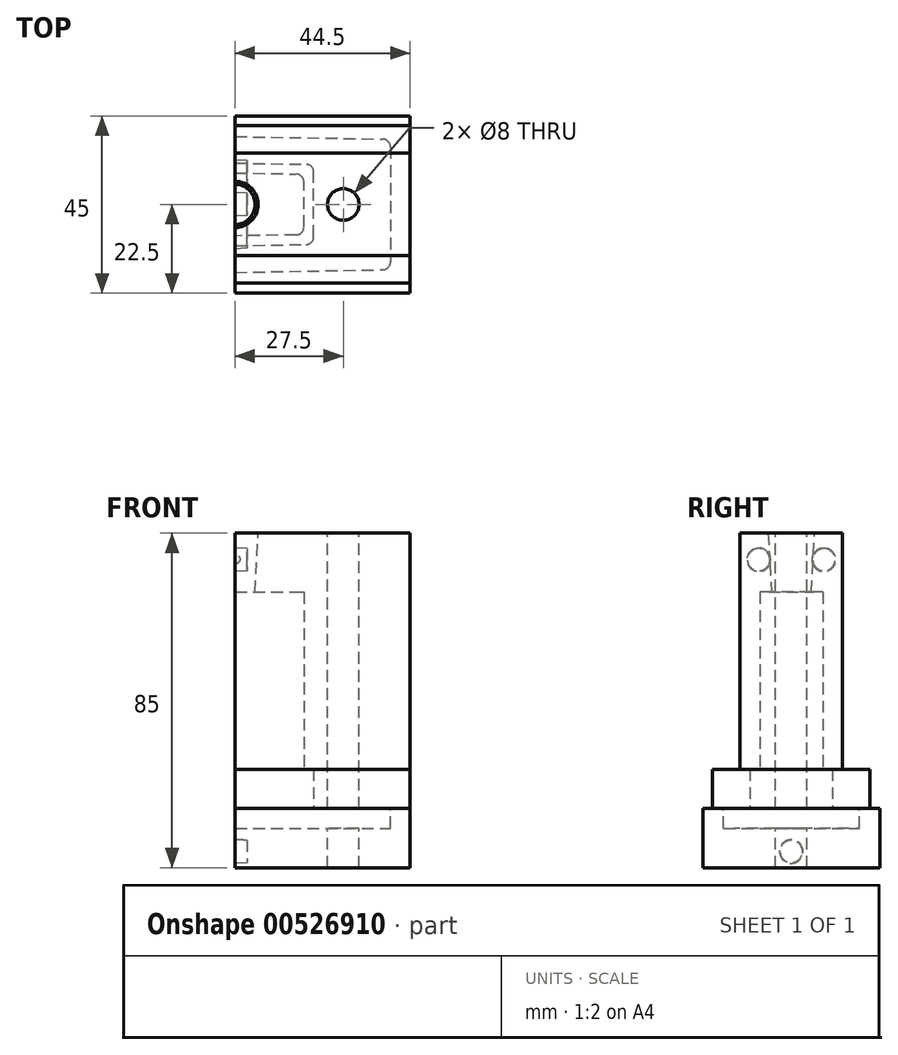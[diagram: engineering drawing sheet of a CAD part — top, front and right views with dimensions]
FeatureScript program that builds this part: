
annotation { "Feature Type Name" : "Feature", "Feature Type Description" : "" }
export const myFeature = defineFeature(function(context is Context, id is Id, definition is map)
    precondition{}
    {
        {
            var Q0;
            Q0=qCreatedBy(makeId("Top.planeOp"),FACE);
            var sketch = newSketch(context, id + "F0", { "sketchPlane" : qUnion([Q0])});
            skLineSegment(sketch, "E0.bottom", {"start": v(44.4, -13) * mm, "end": v(-44.4, -13) * mm});
            skLineSegment(sketch, "E0.top", {"start": v(44.4, 13) * mm, "end": v(-44.4, 13) * mm});
            skLineSegment(sketch, "E0.left", {"start": v(44.4, -13) * mm, "end": v(44.4, 13) * mm});
            skLineSegment(sketch, "E0.right", {"start": v(-44.4, -13) * mm, "end": v(-44.4, 13) * mm});
            skPoint(sketch, "E0.middle", {"position": v(0, 0) * mm});
            skSolve(sketch);
        }
        {
            var Q0;
            Q0=qSketchRegion(id+"F0",true);
            extrude(context, id + "F1", {"entities" : qUnion([Q0]), "depth" : 60 * mm, "offsetDistance" : 25 * mm});
        }
        {
            var Q0;
            Q0=makeQuery(id+"F1.opExtrude","CAP_FACE",FACE,{"disambiguationData":[OSD([sQuery(id+"F0.wireOp",EDGE,"E0.bottom"),sQuery(id+"F0.wireOp",EDGE,"E0.top"),sQuery(id+"F0.wireOp",EDGE,"E0.left"),sQuery(id+"F0.wireOp",EDGE,"E0.right")])],"isStart":true});
            var sketch = newSketch(context, id + "F2", { "sketchPlane" : qUnion([Q0])});
            skPoint(sketch, "E1.middle", {"position": v(0, 0) * mm});
            skLineSegment(sketch, "E2", {"start": v(0, -8) * mm, "end": v(-17.5, -7.7) * mm});
            skLineSegment(sketch, "E3", {"start": v(0, -8) * mm, "end": v(17.5, -7.7) * mm});
            skLineSegment(sketch, "E4", {"start": v(0, 8) * mm, "end": v(-17.5, 7.7) * mm});
            skLineSegment(sketch, "E5", {"start": v(17.5, 7.7) * mm, "end": v(0, 8) * mm});
            skLineSegment(sketch, "E6", {"start": v(-17.5, 7.7) * mm, "end": v(-17.5, -7.7) * mm});
            skLineSegment(sketch, "E7", {"start": v(17.5, 7.7) * mm, "end": v(17.5, -7.7) * mm});
            skSolve(sketch);
        }
        {
            var Q0;
            Q0=qSketchRegion(id+"F2",true);
            extrude(context, id + "F3", {"entities" : qUnion([Q0]), "operationType" : NewBodyOperationType.REMOVE, "oppositeDirection" : true, "depth" : 45 * mm, "offsetDistance" : 25 * mm});
        }
        {
            var Q0;
            Q0=makeQuery(id+"F3.boolean.opBoolean","COPY",EDGE,{"derivedFrom":makeQuery(id+"F3.opExtrude","SWEPT_EDGE",EDGE,{"disambiguationData":[OSD([sQuery(id+"F2.wireOp",EDGE,"E2"),sQuery(id+"F2.wireOp",EDGE,"E6")])]})});
            var Q1;
            Q1=makeQuery(id+"F3.boolean.opBoolean","COPY",EDGE,{"derivedFrom":makeQuery(id+"F3.opExtrude","SWEPT_EDGE",EDGE,{"disambiguationData":[OSD([sQuery(id+"F2.wireOp",EDGE,"E4"),sQuery(id+"F2.wireOp",EDGE,"E6")])]})});
            var Q2;
            Q2=makeQuery(id+"F3.boolean.opBoolean","COPY",EDGE,{"derivedFrom":makeQuery(id+"F3.opExtrude","SWEPT_EDGE",EDGE,{"disambiguationData":[OSD([sQuery(id+"F2.wireOp",EDGE,"E5"),sQuery(id+"F2.wireOp",EDGE,"E7")])]})});
            var Q3;
            Q3=makeQuery(id+"F3.boolean.opBoolean","COPY",EDGE,{"derivedFrom":makeQuery(id+"F3.opExtrude","SWEPT_EDGE",EDGE,{"disambiguationData":[OSD([sQuery(id+"F2.wireOp",EDGE,"E3"),sQuery(id+"F2.wireOp",EDGE,"E7")])]})});
            fillet(context, id + "F4", {"entities" : qUnion([Q0, Q1, Q2, Q3]), "radius" : 2 * mm, "tangentPropagation" : true, "allowEdgeOverflow" : false});
        }
        {
            var Q0;
            Q0=makeQuery(id+"F1.opExtrude","CAP_FACE",FACE,{"disambiguationData":[OSD([sQuery(id+"F0.wireOp",EDGE,"E0.bottom"),sQuery(id+"F0.wireOp",EDGE,"E0.top"),sQuery(id+"F0.wireOp",EDGE,"E0.left"),sQuery(id+"F0.wireOp",EDGE,"E0.right")])],"isStart":true});
            var sketch = newSketch(context, id + "F5", { "sketchPlane" : qUnion([Q0])});
            skLineSegment(sketch, "E8.bottom", {"start": v(44.45, -20) * mm, "end": v(-44.45, -20) * mm});
            skLineSegment(sketch, "E8.top", {"start": v(44.45, 20) * mm, "end": v(-44.45, 20) * mm});
            skLineSegment(sketch, "E8.left", {"start": v(44.45, -20) * mm, "end": v(44.45, 20) * mm});
            skLineSegment(sketch, "E8.right", {"start": v(-44.45, -20) * mm, "end": v(-44.45, 20) * mm});
            skPoint(sketch, "E8.middle", {"position": v(0, 0) * mm});
            skSolve(sketch);
        }
        {
            var Q0;
            Q0=qSketchRegion(id+"F5",true);
            extrude(context, id + "F6", {"entities" : qUnion([Q0]), "operationType" : NewBodyOperationType.ADD, "depth" : 10 * mm, "offsetDistance" : 25 * mm});
        }
        {
            var Q0;
            Q0=makeQuery(id+"F6.opExtrude","CAP_FACE",FACE,{"disambiguationData":[OSD([sQuery(id+"F5.wireOp",EDGE,"E8.bottom"),sQuery(id+"F5.wireOp",EDGE,"E8.top"),sQuery(id+"F5.wireOp",EDGE,"E8.left"),sQuery(id+"F5.wireOp",EDGE,"E8.right")])],"isStart":false});
            var sketch = newSketch(context, id + "F7", { "sketchPlane" : qUnion([Q0])});
            skPoint(sketch, "E9.middle", {"position": v(0, 0) * mm});
            skLineSegment(sketch, "E10", {"start": v(0, -10.5) * mm, "end": v(20, -10.15) * mm});
            skLineSegment(sketch, "E11", {"start": v(0, -10.5) * mm, "end": v(-20, -10.15) * mm});
            skLineSegment(sketch, "E12", {"start": v(-20, 10.15) * mm, "end": v(0, 10.5) * mm});
            skLineSegment(sketch, "E13", {"start": v(0, 10.5) * mm, "end": v(20, 10.15) * mm});
            skLineSegment(sketch, "E14", {"start": v(20, 10.15) * mm, "end": v(20, -10.15) * mm});
            skLineSegment(sketch, "E15", {"start": v(-20, 10.15) * mm, "end": v(-20, -10.15) * mm});
            skSolve(sketch);
        }
        {
            var Q0;
            Q0=qSketchRegion(id+"F7",true);
            extrude(context, id + "F8", {"entities" : qUnion([Q0]), "operationType" : NewBodyOperationType.REMOVE, "oppositeDirection" : true, "depth" : 10 * mm, "offsetDistance" : 25 * mm});
        }
        {
            var Q0;
            Q0=makeQuery(id+"F8.boolean.opBoolean","COPY",EDGE,{"derivedFrom":makeQuery(id+"F8.opExtrude","SWEPT_EDGE",EDGE,{"disambiguationData":[OSD([sQuery(id+"F7.wireOp",EDGE,"E11"),sQuery(id+"F7.wireOp",EDGE,"E15")])]})});
            var Q1;
            Q1=makeQuery(id+"F8.boolean.opBoolean","COPY",EDGE,{"derivedFrom":makeQuery(id+"F8.opExtrude","SWEPT_EDGE",EDGE,{"disambiguationData":[OSD([sQuery(id+"F7.wireOp",EDGE,"E12"),sQuery(id+"F7.wireOp",EDGE,"E15")])]})});
            var Q2;
            Q2=makeQuery(id+"F8.boolean.opBoolean","COPY",EDGE,{"derivedFrom":makeQuery(id+"F8.opExtrude","SWEPT_EDGE",EDGE,{"disambiguationData":[OSD([sQuery(id+"F7.wireOp",EDGE,"E10"),sQuery(id+"F7.wireOp",EDGE,"E14")])]})});
            var Q3;
            Q3=makeQuery(id+"F8.boolean.opBoolean","COPY",EDGE,{"derivedFrom":makeQuery(id+"F8.opExtrude","SWEPT_EDGE",EDGE,{"disambiguationData":[OSD([sQuery(id+"F7.wireOp",EDGE,"E13"),sQuery(id+"F7.wireOp",EDGE,"E14")])]})});
            fillet(context, id + "F9", {"entities" : qUnion([Q0, Q1, Q2, Q3]), "radius" : 2 * mm, "tangentPropagation" : true, "allowEdgeOverflow" : false});
        }
        {
            var Q0;
            Q0=makeQuery(id+"F6.opExtrude","CAP_FACE",FACE,{"disambiguationData":[OSD([sQuery(id+"F5.wireOp",EDGE,"E8.bottom"),sQuery(id+"F5.wireOp",EDGE,"E8.top"),sQuery(id+"F5.wireOp",EDGE,"E8.left"),sQuery(id+"F5.wireOp",EDGE,"E8.right")])],"isStart":false});
            var sketch = newSketch(context, id + "F10", { "sketchPlane" : qUnion([Q0])});
            skLineSegment(sketch, "E16.bottom", {"start": v(44.5, -22.5) * mm, "end": v(-44.5, -22.5) * mm});
            skLineSegment(sketch, "E16.top", {"start": v(44.5, 22.5) * mm, "end": v(-44.5, 22.5) * mm});
            skLineSegment(sketch, "E16.left", {"start": v(44.5, -22.5) * mm, "end": v(44.5, 22.5) * mm});
            skLineSegment(sketch, "E16.right", {"start": v(-44.5, -22.5) * mm, "end": v(-44.5, 22.5) * mm});
            skPoint(sketch, "E16.middle", {"position": v(0, 0) * mm});
            skSolve(sketch);
        }
        {
            var Q0;
            Q0=qSketchRegion(id+"F10",true);
            extrude(context, id + "F11", {"entities" : qUnion([Q0]), "operationType" : NewBodyOperationType.ADD, "depth" : 15 * mm, "offsetDistance" : 25 * mm});
        }
        {
            var Q0;
            {var subQ0=sQuery(id+"F10.wireOp",EDGE,"E16.bottom");var subQ1=sQuery(id+"F10.wireOp",EDGE,"E16.top");var subQ2=sQuery(id+"F10.wireOp",EDGE,"E16.left");var subQ3=sQuery(id+"F10.wireOp",EDGE,"E16.right");Q0=makeQuery(id+"F11.boolean.opBoolean","SPLIT",FACE,{"disambiguationData":[TD([makeQuery(id+"F6.opExtrude","SWEPT_FACE",FACE,{"disambiguationData":[OSD([sQuery(id+"F5.wireOp",EDGE,"E8.bottom")])]})])],"derivedFrom":makeQuery(id+"F11.opExtrude","CAP_FACE",FACE,{"disambiguationData":[OSD([subQ0,subQ1,subQ2,subQ3])],"isStart":true})});}
            var sketch = newSketch(context, id + "F12", { "sketchPlane" : qUnion([Q0])});
            skPoint(sketch, "E17.middle", {"position": v(0, 0) * mm});
            skLineSegment(sketch, "E18", {"start": v(0, -17.25) * mm, "end": v(39.5, -16.56) * mm});
            skLineSegment(sketch, "E19", {"start": v(0, -17.25) * mm, "end": v(-44.45, -17.25) * mm});
            skLineSegment(sketch, "E20", {"start": v(-39.5, -16.56) * mm, "end": v(0, -17.25) * mm});
            skLineSegment(sketch, "E21", {"start": v(0, 17.25) * mm, "end": v(-39.5, 16.56) * mm});
            skLineSegment(sketch, "E22", {"start": v(0, 17.25) * mm, "end": v(39.5, 16.56) * mm});
            skLineSegment(sketch, "E23", {"start": v(-39.5, 16.56) * mm, "end": v(-39.5, -16.56) * mm});
            skLineSegment(sketch, "E24", {"start": v(39.5, 16.56) * mm, "end": v(39.5, -16.56) * mm});
            skSolve(sketch);
        }
        {
            var Q0;
            Q0=qSketchRegion(id+"F12",true);
            extrude(context, id + "F13", {"entities" : qUnion([Q0]), "operationType" : NewBodyOperationType.REMOVE, "oppositeDirection" : true, "depth" : 5 * mm, "offsetDistance" : 25 * mm});
        }
        {
            var Q0;
            Q0=makeQuery(id+"F13.boolean.opBoolean","COPY",EDGE,{"derivedFrom":makeQuery(id+"F13.opExtrude","SWEPT_EDGE",EDGE,{"disambiguationData":[OSD([sQuery(id+"F12.wireOp",EDGE,"E21"),sQuery(id+"F12.wireOp",EDGE,"E23")])]})});
            var Q1;
            Q1=makeQuery(id+"F13.boolean.opBoolean","COPY",EDGE,{"derivedFrom":makeQuery(id+"F13.opExtrude","SWEPT_EDGE",EDGE,{"disambiguationData":[OSD([sQuery(id+"F12.wireOp",EDGE,"E20"),sQuery(id+"F12.wireOp",EDGE,"E23")])]})});
            var Q2;
            Q2=makeQuery(id+"F13.boolean.opBoolean","COPY",EDGE,{"derivedFrom":makeQuery(id+"F13.opExtrude","SWEPT_EDGE",EDGE,{"disambiguationData":[OSD([sQuery(id+"F12.wireOp",EDGE,"E18"),sQuery(id+"F12.wireOp",EDGE,"E24")])]})});
            var Q3;
            Q3=makeQuery(id+"F13.boolean.opBoolean","COPY",EDGE,{"derivedFrom":makeQuery(id+"F13.opExtrude","SWEPT_EDGE",EDGE,{"disambiguationData":[OSD([sQuery(id+"F12.wireOp",EDGE,"E22"),sQuery(id+"F12.wireOp",EDGE,"E24")])]})});
            fillet(context, id + "F14", {"entities" : qUnion([Q0, Q1, Q2, Q3]), "radius" : 2 * mm, "tangentPropagation" : true, "allowEdgeOverflow" : false});
        }
        {
            var Q0;
            Q0=makeQuery(id+"F1.opExtrude","CAP_FACE",FACE,{"disambiguationData":[OSD([sQuery(id+"F0.wireOp",EDGE,"E0.bottom"),sQuery(id+"F0.wireOp",EDGE,"E0.top"),sQuery(id+"F0.wireOp",EDGE,"E0.left"),sQuery(id+"F0.wireOp",EDGE,"E0.right")])],"isStart":false});
            var sketch = newSketch(context, id + "F15", { "sketchPlane" : qUnion([Q0])});
            skCircle(sketch, "E25", {"center": v(27.5, 0) * mm, "radius": 4 * mm});
            skCircle(sketch, "E26", {"center": v(-27.5, 0) * mm, "radius": 4.67 * mm});
            skSolve(sketch);
        }
        {
            var Q0;
            Q0=makeQuery(id+"F15.imprint","IMPRINT",FACE,{"disambiguationData":[TD([[makeQuery(id+"F15.imprint","IMPRINT",EDGE,{"derivedFrom":sQuery(id+"F15.wireOp",EDGE,"E26")}),1.0]])]});
            var Q1;
            Q1=makeQuery(id+"F15.imprint","IMPRINT",FACE,{"disambiguationData":[TD([[makeQuery(id+"F15.imprint","IMPRINT",EDGE,{"derivedFrom":sQuery(id+"F15.wireOp",EDGE,"E25")}),1.0]])]});
            var Q2;
            Q2=sQuery(id+"F15.wireOp",EDGE,"E26");
            var Q3;
            Q3=sQuery(id+"F15.wireOp",EDGE,"E25");
            extrude(context, id + "F16", {"entities" : qUnion([Q0, Q1]), "operationType" : NewBodyOperationType.REMOVE, "surfaceEntities" : qUnion([Q2, Q3]), "endBound" : BoundingType.THROUGH_ALL, "oppositeDirection" : true, "depth" : 90 * mm, "offsetDistance" : 25 * mm});
        }
        {
            var Q0;
            Q0=qCreatedBy(makeId("Right.planeOp"),FACE);
            var sketch = newSketch(context, id + "F17", { "sketchPlane" : qUnion([Q0])});
            skLineSegment(sketch, "E27.bottom", {"start": v(-35.8, 69.27) * mm, "end": v(43.73, 69.27) * mm});
            skLineSegment(sketch, "E27.top", {"start": v(-35.8, -49.53) * mm, "end": v(43.73, -49.53) * mm});
            skLineSegment(sketch, "E27.left", {"start": v(-35.8, 69.27) * mm, "end": v(-35.8, -49.53) * mm});
            skLineSegment(sketch, "E27.right", {"start": v(43.73, 69.27) * mm, "end": v(43.73, -49.53) * mm});
            skSolve(sketch);
        }
        {
            var Q0;
            Q0=qSketchRegion(id+"F17",true);
            extrude(context, id + "F18", {"entities" : qUnion([Q0]), "operationType" : NewBodyOperationType.REMOVE, "oppositeDirection" : true, "depth" : 80 * mm, "offsetDistance" : 25 * mm});
        }
        {
            var Q0;
            Q0=makeQuery(id+"F18.boolean.opBoolean","COPY",FACE,{"derivedFrom":makeQuery(id+"F18.opExtrude","CAP_FACE",FACE,{"disambiguationData":[OSD([sQuery(id+"F17.wireOp",EDGE,"E27.bottom"),sQuery(id+"F17.wireOp",EDGE,"E27.top"),sQuery(id+"F17.wireOp",EDGE,"E27.left"),sQuery(id+"F17.wireOp",EDGE,"E27.right")])],"isStart":true})});
            var sketch = newSketch(context, id + "F19", { "sketchPlane" : qUnion([Q0])});
            skCircle(sketch, "E28", {"center": v(8.28, 53.23) * mm, "radius": 3 * mm});
            skCircle(sketch, "E29", {"center": v(0, -20.9) * mm, "radius": 3 * mm});
            skLineSegment(sketch, "E30", {"start": v(0, 60) * mm, "end": v(0, 81.48) * mm});
            skPoint(sketch, "E30.endSnap0", {"position": v(0, 60) * mm});
            skCircle(sketch, "E31.MirrorC", {"center": v(-8.28, 53.23) * mm, "radius": 3 * mm});
            skSolve(sketch);
        }
        {
            var Q0;
            Q0=qSketchRegion(id+"F19",true);
            extrude(context, id + "F20", {"entities" : qUnion([Q0]), "operationType" : NewBodyOperationType.ADD, "oppositeDirection" : true, "depth" : 3 * mm, "offsetDistance" : 25 * mm, "hasDraft" : true, "draftAngle" : 3 * degree});
        }
        {
            var Q0;
            Q0=qSketchRegion(id+"F19",true);
            extrude(context, id + "F21", {"entities" : qUnion([Q0]), "operationType" : NewBodyOperationType.REMOVE, "oppositeDirection" : true, "depth" : 3 * mm, "offsetDistance" : 25 * mm, "hasDraft" : true, "draftAngle" : 3 * degree, "draftPullDirection" : true});
        }
        {
            var Q0;
            Q0=makeQuery(id+"F3.boolean.opBoolean","COPY",FACE,{"derivedFrom":makeQuery(id+"F3.opExtrude","CAP_FACE",FACE,{"disambiguationData":[OSD([sQuery(id+"F2.wireOp",EDGE,"E2"),sQuery(id+"F2.wireOp",EDGE,"E3"),sQuery(id+"F2.wireOp",EDGE,"E4"),sQuery(id+"F2.wireOp",EDGE,"E5"),sQuery(id+"F2.wireOp",EDGE,"E6"),sQuery(id+"F2.wireOp",EDGE,"E7")])],"isStart":false})});
            var sketch = newSketch(context, id + "F22", { "sketchPlane" : qUnion([Q0])});
            skCircle(sketch, "E32", {"center": v(0, 0) * mm, "radius": 5.09 * mm});
            skSolve(sketch);
        }
        {
            var Q0;
            Q0=qSketchRegion(id+"F22",true);
            extrude(context, id + "F23", {"entities" : qUnion([Q0]), "operationType" : NewBodyOperationType.REMOVE, "oppositeDirection" : true, "depth" : 25 * mm, "offsetDistance" : 25 * mm, "hasDraft" : true, "draftAngle" : 3 * degree});
        }
    });
